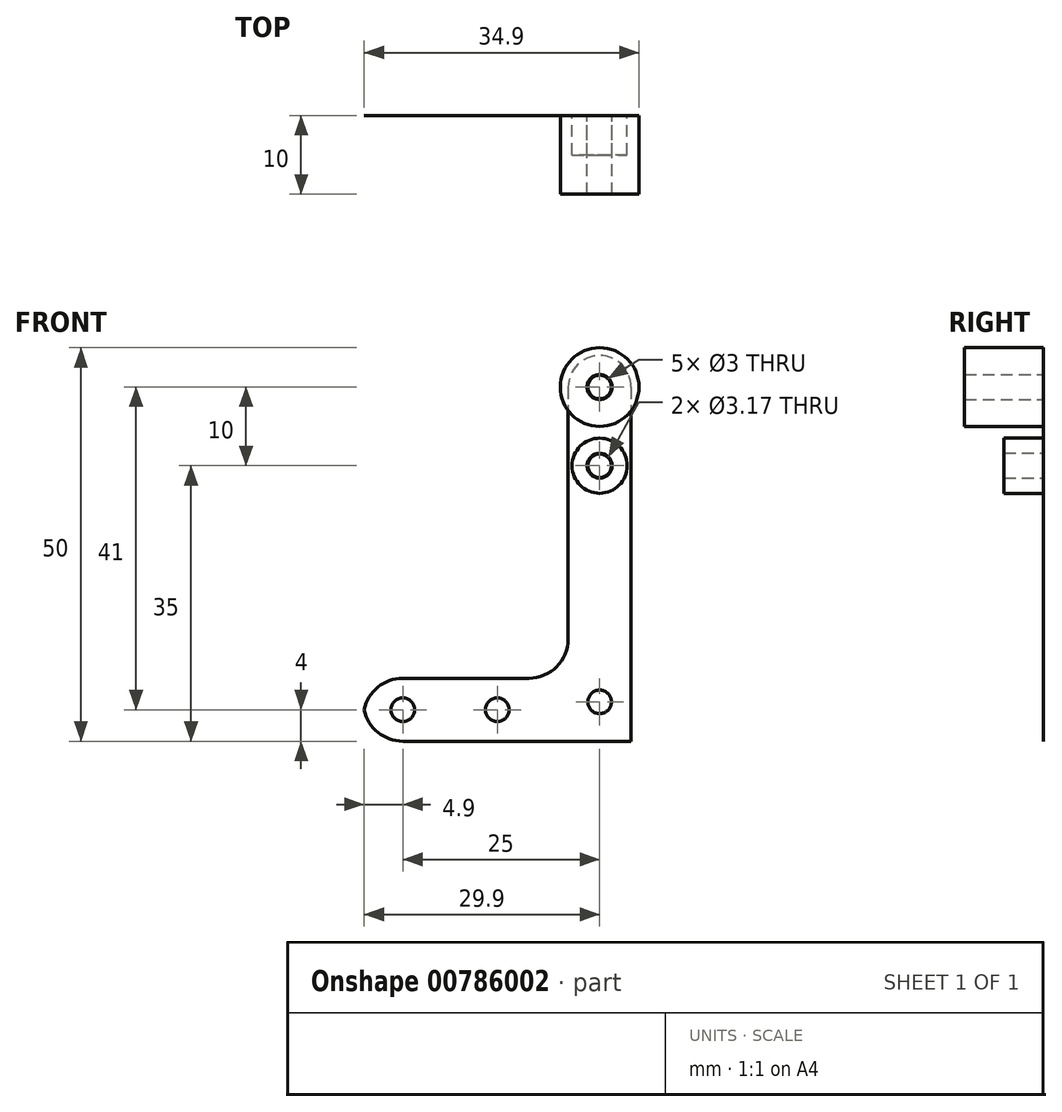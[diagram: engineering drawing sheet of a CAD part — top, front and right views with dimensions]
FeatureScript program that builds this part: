
annotation { "Feature Type Name" : "Feature", "Feature Type Description" : "" }
export const myFeature = defineFeature(function(context is Context, id is Id, definition is map)
    precondition{}
    {
        {
            var Q0;
            Q0=qCreatedBy(makeId("Front.planeOp"),FACE);
            var sketch = newSketch(context, id + "F0", { "sketchPlane" : qUnion([Q0])});
            skCircle(sketch, "E0", {"center": v(0, 10) * mm, "radius": 1.5 * mm});
            skCircle(sketch, "E1", {"center": v(0, 0) * mm, "radius": 1.5 * mm});
            skCircle(sketch, "E2", {"center": v(0, -30) * mm, "radius": 1.5 * mm});
            skLineSegment(sketch, "E3.bottom", {"start": v(-4, 35) * mm, "end": v(4, 35) * mm});
            skLineSegment(sketch, "E3.top", {"start": v(-4, -35) * mm, "end": v(4, -35) * mm});
            skLineSegment(sketch, "E3.left", {"start": v(-4, 35) * mm, "end": v(-4, -35) * mm});
            skLineSegment(sketch, "E3.right", {"start": v(4, 35) * mm, "end": v(4, -35) * mm});
            skCircle(sketch, "E4", {"center": v(0, 10) * mm, "radius": 4 * mm});
            skLineSegment(sketch, "E5.bottom", {"start": v(4, -27) * mm, "end": v(-30, -27) * mm});
            skLineSegment(sketch, "E5.top", {"start": v(4, -35) * mm, "end": v(-30, -35) * mm});
            skLineSegment(sketch, "E5.left", {"start": v(4, -27) * mm, "end": v(4, -35) * mm});
            skLineSegment(sketch, "E5.right", {"start": v(-30, -27) * mm, "end": v(-30, -35) * mm});
            skCircle(sketch, "E6", {"center": v(-25, -31) * mm, "radius": 1.5 * mm});
            skPoint(sketch, "E6.centerSnap0", {"position": v(-30, -31) * mm});
            skCircle(sketch, "E7", {"center": v(-13, -31) * mm, "radius": 1.5 * mm});
            skPoint(sketch, "E7.centerSnap0", {"position": v(-13, -27) * mm});
            skSolve(sketch);
        }
        {
            var Q0;
            Q0=makeQuery(id+"F0.imprint","IMPRINT",FACE,{"disambiguationData":[TD([[makeQuery(id+"F0.imprint","IMPRINT",EDGE,{"derivedFrom":sQuery(id+"F0.wireOp",EDGE,"E0")}),-1.0]])]});
            var Q1;
            Q1=makeQuery(id+"F0.imprint","IMPRINT",FACE,{"disambiguationData":[TD([[makeQuery(id+"F0.imprint","IMPRINT",EDGE,{"derivedFrom":sQuery(id+"F0.wireOp",EDGE,"E1")}),-1.0]])]});
            var Q2;
            Q2=makeQuery(id+"F0.imprint","IMPRINT",FACE,{"disambiguationData":[TD([[makeQuery(id+"F0.imprint","IMPRINT",EDGE,{"derivedFrom":sQuery(id+"F0.wireOp",EDGE,"E2")}),-1.0]])]});
            var Q3;
            {var subQ3=sQuery(id+"F0.wireOp",EDGE,"E5.right");Q3=makeQuery(id+"F0.imprint","IMPRINT",FACE,{"disambiguationData":[TD([[makeQuery(id+"F0.imprint","IMPRINT",EDGE,{"derivedFrom":subQ3}),1.0]])]});}
            extrude(context, id + "F1", {"entities" : qUnion([Q0, Q1, Q2, Q3]), "depth" : 1 / 203.2 * mm, "offsetDistance" : 25 * mm});
        }
        {
            var Q0;
            Q0=makeQuery(id+"F1.opExtrude","SWEPT_EDGE",EDGE,{"disambiguationData":[OSD([sQuery(id+"F0.wireOp",EDGE,"E3.left"),sQuery(id+"F0.wireOp",EDGE,"E5.bottom")])]});
            var Q1;
            Q1=makeQuery(id+"F1.opExtrude","SWEPT_EDGE",EDGE,{"disambiguationData":[OSD([sQuery(id+"F0.wireOp",EDGE,"E5.top"),sQuery(id+"F0.wireOp",EDGE,"E5.left")])]});
            var Q2;
            Q2=makeQuery(id+"F1.opExtrude","SWEPT_EDGE",EDGE,{"disambiguationData":[OSD([sQuery(id+"F0.wireOp",EDGE,"E5.bottom"),sQuery(id+"F0.wireOp",EDGE,"E5.right")])]});
            var Q3;
            Q3=makeQuery(id+"F1.opExtrude","SWEPT_EDGE",EDGE,{"disambiguationData":[OSD([sQuery(id+"F0.wireOp",EDGE,"E5.top"),sQuery(id+"F0.wireOp",EDGE,"E5.right")])]});
            fillet(context, id + "F2", {"entities" : qUnion([Q0, Q1, Q2, Q3]), "radius" : 5 * mm, "tangentPropagation" : true, "allowEdgeOverflow" : false});
        }
        {
            var Q0;
            Q0=makeQuery(id+"F1.opExtrude","CAP_FACE",FACE,{"disambiguationData":[OSD([sQuery(id+"F0.wireOp",EDGE,"E0"),sQuery(id+"F0.wireOp",EDGE,"E1"),sQuery(id+"F0.wireOp",EDGE,"E2"),sQuery(id+"F0.wireOp",EDGE,"E3.left"),sQuery(id+"F0.wireOp",EDGE,"E3.right"),sQuery(id+"F0.wireOp",EDGE,"E4"),sQuery(id+"F0.wireOp",EDGE,"E5.bottom"),sQuery(id+"F0.wireOp",EDGE,"E5.top"),sQuery(id+"F0.wireOp",EDGE,"E5.left"),sQuery(id+"F0.wireOp",EDGE,"E5.right"),sQuery(id+"F0.wireOp",EDGE,"E6"),sQuery(id+"F0.wireOp",EDGE,"E7")])],"isStart":false});
            var sketch = newSketch(context, id + "F3", { "sketchPlane" : qUnion([Q0])});
            skCircle(sketch, "E8", {"center": v(0, 10) * mm, "radius": 5 * mm});
            skCircle(sketch, "E9", {"center": v(0, 10) * mm, "radius": 1.59 * mm});
            skSolve(sketch);
        }
        {
            var Q0;
            Q0=qSketchRegion(id+"F3",true);
            extrude(context, id + "F4", {"entities" : qUnion([Q0]), "depth" : 10 * mm, "offsetDistance" : 25 * mm});
        }
        {
            var Q0;
            Q0=makeQuery(id+"F1.opExtrude","CAP_FACE",FACE,{"disambiguationData":[OSD([sQuery(id+"F0.wireOp",EDGE,"E0"),sQuery(id+"F0.wireOp",EDGE,"E1"),sQuery(id+"F0.wireOp",EDGE,"E2"),sQuery(id+"F0.wireOp",EDGE,"E3.left"),sQuery(id+"F0.wireOp",EDGE,"E3.right"),sQuery(id+"F0.wireOp",EDGE,"E4"),sQuery(id+"F0.wireOp",EDGE,"E5.bottom"),sQuery(id+"F0.wireOp",EDGE,"E5.top"),sQuery(id+"F0.wireOp",EDGE,"E5.left"),sQuery(id+"F0.wireOp",EDGE,"E5.right"),sQuery(id+"F0.wireOp",EDGE,"E6"),sQuery(id+"F0.wireOp",EDGE,"E7")])],"isStart":false});
            var sketch = newSketch(context, id + "F5", { "sketchPlane" : qUnion([Q0])});
            skCircle(sketch, "E10", {"center": v(0, 0) * mm, "radius": 1.59 * mm});
            skCircle(sketch, "E11", {"center": v(0, 0) * mm, "radius": 3.5 * mm});
            skSolve(sketch);
        }
        {
            var Q0;
            Q0=qSketchRegion(id+"F5",true);
            extrude(context, id + "F6", {"entities" : qUnion([Q0]), "depth" : 5 * mm, "offsetDistance" : 25 * mm});
        }
    });
